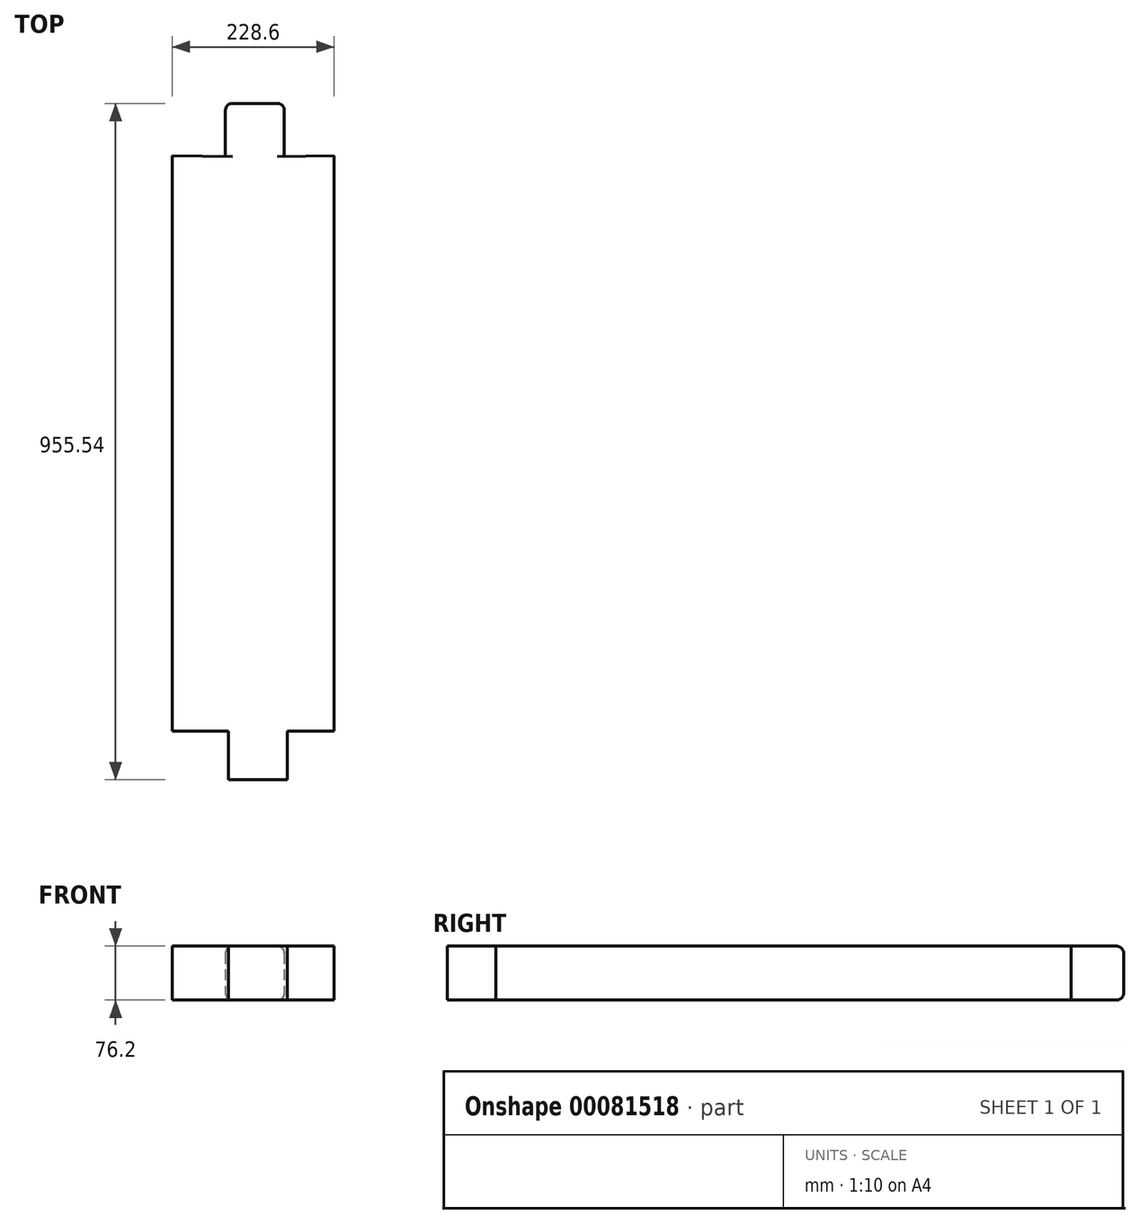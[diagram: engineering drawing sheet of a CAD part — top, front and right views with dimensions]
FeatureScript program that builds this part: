
annotation { "Feature Type Name" : "Feature", "Feature Type Description" : "" }
export const myFeature = defineFeature(function(context is Context, id is Id, definition is map)
    precondition{}
    {
        {
            var Q0;
            Q0=qCreatedBy(makeId("Top.planeOp"),FACE);
            var sketch = newSketch(context, id + "F0", { "sketchPlane" : qUnion([Q0])});
            skLineSegment(sketch, "E0.left", {"start": v(0, 812.8) * mm, "end": v(0, 0) * mm});
            skLineSegment(sketch, "E0.right", {"start": v(228.6, 812.8) * mm, "end": v(228.6, 0) * mm});
            skLineSegment(sketch, "E1", {"start": v(75.05, 886.85) * mm, "end": v(158.32, 886.85) * mm});
            skLineSegment(sketch, "E2", {"start": v(75.05, 886.85) * mm, "end": v(75.05, 811.9) * mm});
            skLineSegment(sketch, "E3", {"start": v(75.05, 811.9) * mm, "end": v(0, 812.8) * mm});
            skLineSegment(sketch, "E4", {"start": v(158.32, 886.85) * mm, "end": v(158.32, 811.9) * mm});
            skLineSegment(sketch, "E5", {"start": v(158.32, 811.9) * mm, "end": v(228.6, 812.8) * mm});
            skLineSegment(sketch, "E6", {"start": v(0, 0) * mm, "end": v(79.21, 0) * mm});
            skLineSegment(sketch, "E7", {"start": v(79.21, 0) * mm, "end": v(79.21, -68.69) * mm});
            skLineSegment(sketch, "E8", {"start": v(79.21, -68.69) * mm, "end": v(162.48, -68.69) * mm});
            skLineSegment(sketch, "E9", {"start": v(162.48, -68.69) * mm, "end": v(162.48, 0) * mm});
            skLineSegment(sketch, "E10", {"start": v(162.48, 0) * mm, "end": v(228.6, 0) * mm});
            skSolve(sketch);
        }
        {
            var Q0;
            Q0 = qSketchRegion(id + "F0", true);
            extrude(context, id + "F1", {"entities" : qUnion([Q0]), "depth" : 76.2 * mm});
        }
        {
            var Q0;
            Q0=makeQuery(id+"F1.opExtrude","SWEPT_EDGE",EDGE,{"disambiguationData":[OSD([sQuery(id+"F0.wireOp",EDGE,"E1"),sQuery(id+"F0.wireOp",EDGE,"E2")])]});
            var Q1;
            Q1=makeQuery(id+"F1.opExtrude","CAP_EDGE",EDGE,{"disambiguationData":[OSD([sQuery(id+"F0.wireOp",EDGE,"E1")])],"isStart":false});
            var Q2;
            Q2=makeQuery(id+"F1.opExtrude","CAP_EDGE",EDGE,{"disambiguationData":[OSD([sQuery(id+"F0.wireOp",EDGE,"E2")])],"isStart":false});
            var Q3;
            Q3=makeQuery(id+"F1.opExtrude","CAP_EDGE",EDGE,{"disambiguationData":[OSD([sQuery(id+"F0.wireOp",EDGE,"E4")])],"isStart":false});
            var Q4;
            Q4=makeQuery(id+"F1.opExtrude","SWEPT_EDGE",EDGE,{"disambiguationData":[OSD([sQuery(id+"F0.wireOp",EDGE,"E1"),sQuery(id+"F0.wireOp",EDGE,"E4")])]});
            var Q5;
            Q5=makeQuery(id+"F1.opExtrude","CAP_EDGE",EDGE,{"disambiguationData":[OSD([sQuery(id+"F0.wireOp",EDGE,"E1")])],"isStart":true});
            var Q6;
            Q6=makeQuery(id+"F1.opExtrude","CAP_EDGE",EDGE,{"disambiguationData":[OSD([sQuery(id+"F0.wireOp",EDGE,"E2")])],"isStart":true});
            var Q7;
            Q7=makeQuery(id+"F1.opExtrude","CAP_EDGE",EDGE,{"disambiguationData":[OSD([sQuery(id+"F0.wireOp",EDGE,"E4")])],"isStart":true});
            fillet(context, id + "F2", {"entities" : qUnion([Q0, Q1, Q2, Q3, Q4, Q5, Q6, Q7]), "radius" : 10 * mm, "tangentPropagation" : true, "allowEdgeOverflow" : false});
        }
    });
